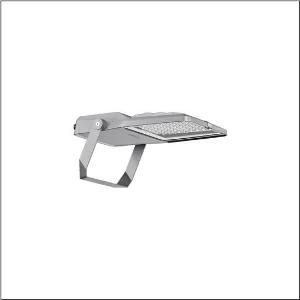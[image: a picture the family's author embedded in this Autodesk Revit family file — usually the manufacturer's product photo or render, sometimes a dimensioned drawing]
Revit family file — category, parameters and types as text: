
# Revit family: floodlight_fl_21_iq_mini___pl43_5xa7771d2a1a_9b6a
name_source: partatom
category: Lighting Fixtures
units: mm (PartAtom-declared; Revit-internal decimal feet)

## family parameters
Cut with Voids When Loaded = No
Host = Face
Light Source = No
Part Type = Normal
Room Calculation Point = No
Round Connector Dimension = Use Diameter
Shared = No

## types (1)
- --- (1 x LED, 18290 lm, 143 W, 3000K)
    Apparent Load = 143 VA
    CIE Flux Codes = 27 78 99 100 100
    Color Rendering = 70
    Color Temperature = 3000K
    Default Elevation = 1800 mm
    Description = Floodlight FL 21 iQ mini, floodlight, primary light control with lens, of PMMA, primary optical cover: protective disc, of toughened safety glass, transparent, light distribution: PL43, light emission: direct distribution, installation type: surface-mounted, LED, High Power LED, rated luminous flux: 18.290lm, luminous efficacy: 128lm/W, light colour: 730, colour temperature: 3000K, control: Auto-Match, Temp-Guard, Lumen-Switch, Night-Set, Smart-Wire, Light-Fading, Desk-Remote (wireless, voltage-free reading and setting of iQ features in the workshop via application-optimized NFC function/RFID function), optimised constant luminous flux control (CLO 2.0), with terminal, 6-pole, mains connection: 220..240V, AC, 50/60Hz, start of lifetime: 143W, end of service life: 152W, reduction: 61W, luminaire housing, of diecast aluminium, powder-coated, Siteco® metallic grey (DB 702S), corrosivity category C5 mid according to DIN EN ISO 12944, sealing non-destructively replaceable, mounting bracket, of steel, galvanised, powder-coated, Siteco® metallic grey (DB 702S), protection rating (complete): IP66, insulation class (complete): insulation class II (safety insulation), certification: CE, ENEC, VDE, protection symbol: D, impact resistance: IK08, permissible operating ambient temperature: -40..+40°C, permissible operating ambient temperature for outdoor applications: -40..+50°C, standard: DIN EN 12944, LABS conformity tested according to VDMA 24364:2018-05, packaging unit: 1 piece

Light Distribution: PL43
    Height = 70 mm
    Lamp = 1 x LED
    Lamp Light Flux = 18290 lm
    Lamp Power = 143 W
    Lamp count = 1
    Length = 485 mm
    Luminous efficacy = 128 lm/W
    Manufacturer = Siteco
    ModVariant = No
    Model = 5XA7771D2A1A
    Number of Poles = 1
    OnlyDefault = Yes
    Power Factor = 1
    Product Name = Floodlight FL 21 iQ mini | PL43
    Product group = floodlight | pylon annexe
    ProductGroupID = 6200
    Protection Class = Protection class II
    Protection Degree = IP 66
    RLX_Detail_Level = 1
    RLX_Emergency_Light_Flux = 0 lm
    RLX_Emergency_Type = 0
    RLX_Emergency_Type_DB = No
    RlxData = <blob elided: 96377 chars, md5=9898e39c>
    Socket = socket
    Standby Power = 0 W
    System Light Flux = 18290 lm
    System Power = 143 W
    Type Comments = factory setting: luminous flux: 100 % | dim-lin: 254 | 730 mA
    Type Image = l_1006845.jpg
    URL = http://relux.com
    VarID = @adj_094387
    Voltage = 0 V
    Weight = 0.00 kg
    Width = 337 mm

## geometry (parser evidence)
native form markers: Blend x4, Sweep x11
no freeform markers — native parametric forms only
